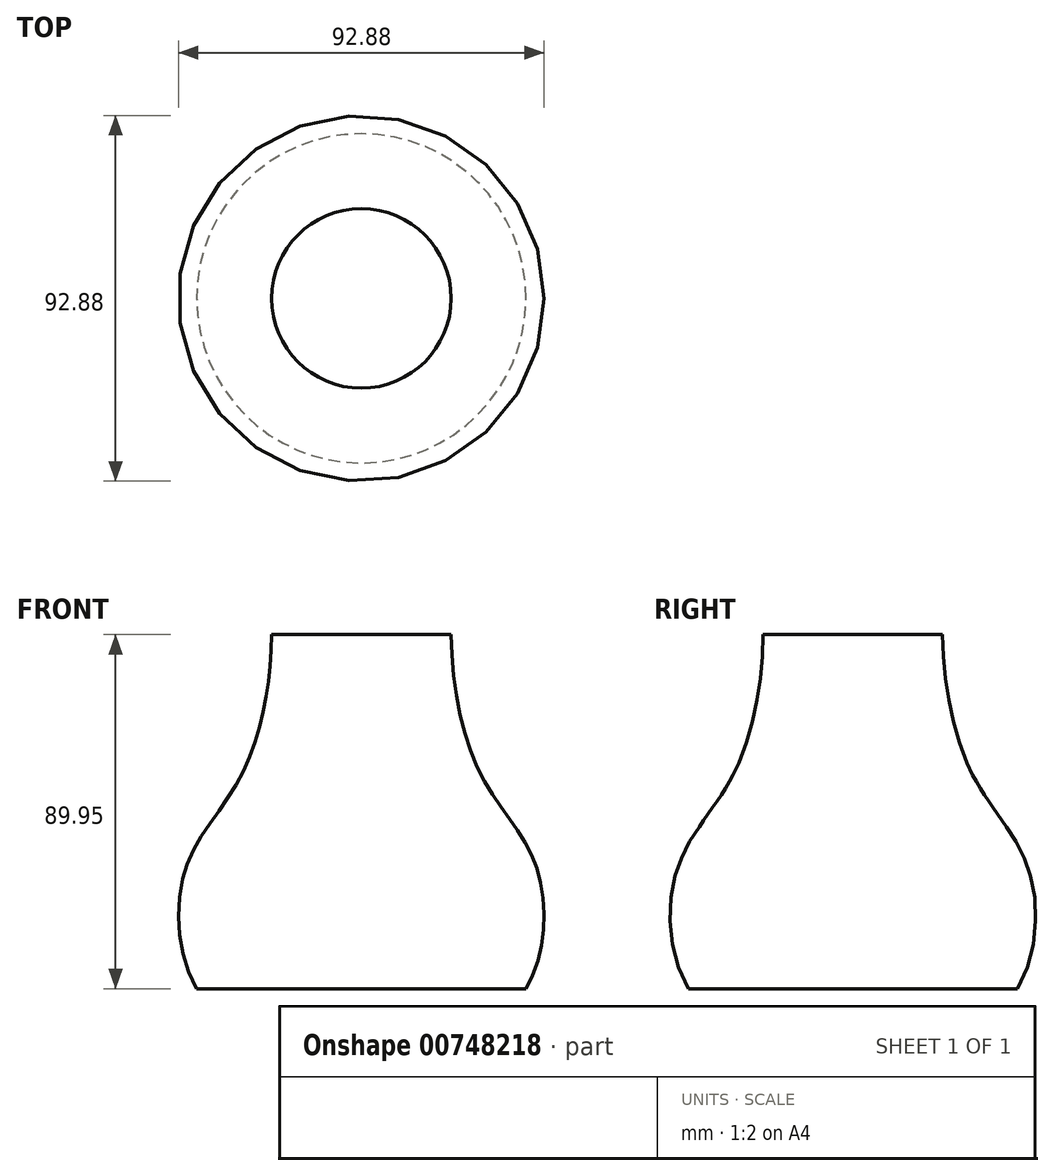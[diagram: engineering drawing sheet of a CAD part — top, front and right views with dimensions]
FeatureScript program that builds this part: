
annotation { "Feature Type Name" : "Feature", "Feature Type Description" : "" }
export const myFeature = defineFeature(function(context is Context, id is Id, definition is map)
    precondition{}
    {
        {
            var Q0;
            Q0=qCreatedBy(makeId("Front.planeOp"),FACE);
            var sketch = newSketch(context, id + "F0", { "sketchPlane" : qUnion([Q0])});
            skFitSpline(sketch, "E0", {"points": [v(24.03, 54.39) * mm, v(29.37, 5.2) * mm, v(44.27, -19.82) * mm, v(42.3, -50.45) * mm, v(20.38, -69) * mm], "startDerivative": vector(-27.97, -156.62) * mm, "endDerivative": vector(-110.3, -67.03) * mm});
            skLineSegment(sketch, "E1", {"start": v(-20.38, 38.65) * mm, "end": v(43.99, 38.65) * mm});
            skLineSegment(sketch, "E2", {"start": v(-18.7, -51.3) * mm, "end": v(60.3, -51.3) * mm});
            skLineSegment(sketch, "E3", {"start": v(0, 56.36) * mm, "end": v(0, -66.47) * mm});
            skSolve(sketch);
        }
        {
            var Q0;
            {var subQ0=sQuery(id+"F0.wireOp",EDGE,"E1");var subQ1=sQuery(id+"F0.wireOp",EDGE,"E0");var subQ2=makeQuery(id+"F0.imprint","INTERSECT",VERTEX,{"derivedFrom":[subQ1,subQ0]});Q0=makeQuery(id+"F0.imprint","IMPRINT",FACE,{"disambiguationData":[TD([[makeQuery(id+"F0.imprint","IMPRINT",EDGE,{"disambiguationData":[TD([[subQ2,-1.0]])],"derivedFrom":subQ1}),-1.0]])]});}
            var Q1;
            Q1=sQuery(id+"F0.wireOp",EDGE,"E3");
            revolve(context, id + "F1", {"surfaceOperationType" : NewSurfaceOperationType.NEW, "entities" : qUnion([Q0]), "axis" : qUnion([Q1]), "revolveType" : RevolveType.FULL});
        }
    });
